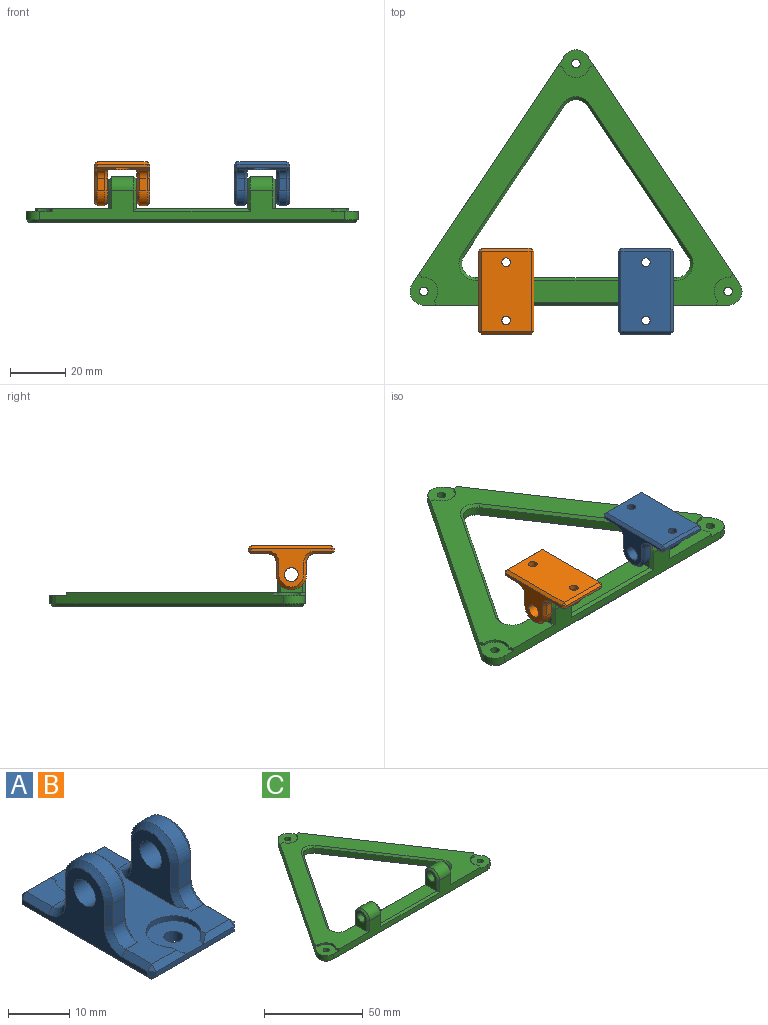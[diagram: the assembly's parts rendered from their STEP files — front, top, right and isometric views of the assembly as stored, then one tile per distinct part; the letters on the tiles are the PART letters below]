
ASSEMBLY  parts=3 mates=5
PART A: 74 faces, bbox 20.7x33.9x16.7 mm
  f0: bspline ~5.16x3.38mm, area 1.7mm2, adj f11,f19,f20,f35
  f1: bspline ~5.16x3.38mm, area 1.7mm2, adj f11,f22,f23,f56
  f2: plane 7.27x1.01mm, normal (0,0.71,0.71), area 8.9mm2, adj f11,f14,f38,f73
  f3: plane 7.27x1.01mm, normal (0,-0.71,0.71), area 8.9mm2, adj f11,f12,f53,f72
  f4: plane 4.5x2.75mm, normal (0,1,0), area 12.4mm2, adj f6,f26,f52,f68
  f5: plane 4.5x2.75mm, normal (0,-1,0), area 12.4mm2, adj f6,f27,f58,f70
  f6: cylinder r=5.5mm len=11mm, axis (-1,0,0), area 47.5mm2, adj f4,f5,f55,f69
  f7: cylinder r=2.5mm len=5mm, axis (-1,0,0), area 74.6mm2, adj f17,f24
  f8: plane 4.5x2.75mm, normal (0,1,0), area 12.4mm2, adj f9,f28,f33,f63
  f9: cylinder r=5.5mm len=11mm, axis (-1,0,0), area 47.5mm2, adj f8,f10,f36,f64
  f10: plane 4.5x2.75mm, normal (0,-1,0), area 12.4mm2, adj f9,f29,f39,f65
  f11: plane 29.74x18.74mm, normal (0,0,1), area 274.6mm2, adj f0,f1,f2,f3,f20,f23,f24,f25
  f12: plane 18x1mm, normal (0,-1,0), area 18mm2, adj f3,f22,f49,f50,f56,f57
  f13: plane 29x18mm, normal (0,0,-1), area 506.9mm2, adj f18,f21,f40,f41,f50,f51
  f14: plane 18x1mm, normal (0,1,0), area 18mm2, adj f2,f19,f34,f35,f41,f42
  f15: cylinder r=2.5mm len=5mm, axis (-1,0,0), area 74.6mm2, adj f16,f25
  f16: plane 29x14mm, normal (1,0,0), area 124.5mm2, adj f15,f30,f31,f33,f34,f36,f39,f40
  f17: plane 29x14mm, normal (-1,0,0), area 124.5mm2, adj f7,f42,f43,f47,f51,f52,f55,f57
  f18: cylinder r=1.55mm len=3.1mm, axis (0,0,1), area 19.5mm2, adj f13,f19
  f19: plane 9.6x9.08mm, normal (0,0,1), area 58.7mm2, adj f0,f14,f18,f20,f73
  f20: cylinder r=4.5mm len=9mm, axis (0,0,1), area 22.2mm2, adj f0,f11,f19,f73
  f21: cylinder r=1.55mm len=3.1mm, axis (0,0,1), area 19.5mm2, adj f13,f22
  f22: plane 9.6x9.08mm, normal (0,0,1), area 58.7mm2, adj f1,f12,f21,f23,f72
  f23: cylinder r=4.5mm len=9mm, axis (0,0,1), area 22.2mm2, adj f1,f11,f22,f72
  f24: plane 12x11.71mm, normal (1,0,0), area 82.2mm2, adj f7,f11,f67,f68,f69,f70,f71
  f25: plane 12x11.71mm, normal (-1,0,0), area 82.2mm2, adj f11,f15,f62,f63,f64,f65,f66
  f26: cylinder r=3mm len=3mm, axis (-1,0,0), area 13mm2, adj f4,f11,f47,f67
  f27: cylinder r=3mm len=3mm, axis (1,0,0), area 13mm2, adj f5,f11,f60,f71
  f28: cylinder r=3mm len=3mm, axis (-1,0,0), area 13mm2, adj f8,f11,f31,f62
  f29: cylinder r=3mm len=3mm, axis (1,0,0), area 13mm2, adj f10,f11,f44,f66
  f30: plane 6x1mm, normal (0.71,0,0.71), area 8.5mm2, adj f11,f16,f31,f32
  f31: cone r=4mm half-angle=45deg, axis (1,0,0), area 7.8mm2, adj f16,f28,f30,f33
  f32: plane 1x1mm, normal (0.58,0.58,0.58), area 0.9mm2, adj f30,f34,f35
  f33: plane 4.5x1mm, normal (0.71,0.71,0), area 6.4mm2, adj f8,f16,f31,f36
  f34: plane 1x1mm, normal (0.71,0.71,0), area 1.4mm2, adj f14,f16,f32,f37
  f35: plane 7.27x1.01mm, normal (0,0.71,0.71), area 8.9mm2, adj f0,f11,f14,f32
  f36: cone r=5.5mm half-angle=45deg, axis (-1,0,0), area 22.2mm2, adj f9,f16,f33,f39
  f37: plane 1x1mm, normal (0.58,0.58,-0.58), area 0.9mm2, adj f34,f40,f41
  f38: plane 1x1mm, normal (-0.58,0.58,0.58), area 0.9mm2, adj f2,f42,f43
  f39: plane 4.5x1mm, normal (0.71,-0.71,0), area 6.4mm2, adj f10,f16,f36,f44
  f40: plane 29x1mm, normal (0.71,0,-0.71), area 41mm2, adj f13,f16,f37,f45
  f41: plane 18x1mm, normal (0,0.71,-0.71), area 25.5mm2, adj f13,f14,f37,f46
  f42: plane 1x1mm, normal (-0.71,0.71,0), area 1.4mm2, adj f14,f17,f38,f46
  f43: plane 6x1mm, normal (-0.71,0,0.71), area 8.5mm2, adj f11,f17,f38,f47
  f44: cone r=4mm half-angle=45deg, axis (1,0,0), area 7.8mm2, adj f16,f29,f39,f48
  f45: plane 1x1mm, normal (0.58,-0.58,-0.58), area 0.9mm2, adj f40,f49,f50
  f46: plane 1x1mm, normal (-0.58,0.58,-0.58), area 0.9mm2, adj f41,f42,f51
  f47: cone r=4mm half-angle=45deg, axis (-1,0,0), area 7.8mm2, adj f17,f26,f43,f52
  f48: plane 6x1mm, normal (0.71,0,0.71), area 8.5mm2, adj f11,f16,f44,f53
  f49: plane 1x1mm, normal (0.71,-0.71,0), area 1.4mm2, adj f12,f16,f45,f53
  f50: plane 18x1mm, normal (0,-0.71,-0.71), area 25.5mm2, adj f12,f13,f45,f54
  f51: plane 29x1mm, normal (-0.71,0,-0.71), area 41mm2, adj f13,f17,f46,f54
  f52: plane 4.5x1mm, normal (-0.71,0.71,0), area 6.4mm2, adj f4,f17,f47,f55
  f53: plane 1x1mm, normal (0.58,-0.58,0.58), area 0.9mm2, adj f3,f48,f49
  f54: plane 1x1mm, normal (-0.58,-0.58,-0.58), area 0.9mm2, adj f50,f51,f57
  f55: cone r=4.5mm half-angle=45deg, axis (1,0,0), area 22.2mm2, adj f6,f17,f52,f58
  f56: plane 7.27x1.01mm, normal (0,-0.71,0.71), area 8.9mm2, adj f1,f11,f12,f59
  f57: plane 1x1mm, normal (-0.71,-0.71,0), area 1.4mm2, adj f12,f17,f54,f59
  f58: plane 4.5x1mm, normal (-0.71,-0.71,0), area 6.4mm2, adj f5,f17,f55,f60
  f59: plane 1x1mm, normal (-0.58,-0.58,0.58), area 0.9mm2, adj f56,f57,f61
  f60: cone r=4mm half-angle=45deg, axis (-1,0,0), area 7.8mm2, adj f17,f27,f58,f61
  f61: plane 6x1mm, normal (-0.71,0,0.71), area 8.5mm2, adj f11,f17,f59,f60
  f62: cone r=4mm half-angle=45deg, axis (-1,0,0), area 5.9mm2, adj f11,f25,f28,f63
  f63: plane 4.5x1mm, normal (-0.71,0.71,0), area 6.4mm2, adj f8,f25,f62,f64
  f64: cone r=4.5mm half-angle=45deg, axis (1,0,0), area 22.2mm2, adj f9,f25,f63,f65
  f65: plane 4.5x1mm, normal (-0.71,-0.71,0), area 6.4mm2, adj f10,f25,f64,f66
  f66: cone r=4mm half-angle=45deg, axis (-1,0,0), area 5.9mm2, adj f11,f25,f29,f65
  f67: cone r=4mm half-angle=45deg, axis (1,0,0), area 5.9mm2, adj f11,f24,f26,f68
  f68: plane 4.5x1mm, normal (0.71,0.71,0), area 6.4mm2, adj f4,f24,f67,f69
  f69: cone r=5.5mm half-angle=45deg, axis (-1,0,0), area 22.2mm2, adj f6,f24,f68,f70
  f70: plane 4.5x1mm, normal (0.71,-0.71,0), area 6.4mm2, adj f5,f24,f69,f71
  f71: cone r=4mm half-angle=45deg, axis (1,0,0), area 5.9mm2, adj f11,f24,f27,f70
  f72: bspline ~5.16x3.38mm, area 1.7mm2, adj f3,f11,f22,f23
  f73: bspline ~5.16x3.38mm, area 1.7mm2, adj f2,f11,f19,f20
PART B: same geometry as A
PART C: 74 faces, bbox 120x92.3x16.5 mm
  f0: plane 72.58x10.5mm, normal (0,1,0), area 337.7mm2, adj f2,f4,f13,f25,f34,f35,f43,f44
  f1: plane 110x10.5mm, normal (0,-1,0), area 493.1mm2, adj f2,f10,f11,f14,f17,f23,f25,f32
  f2: cylinder r=5mm len=10mm, axis (-1,0,0), area 125.7mm2, adj f0,f1,f41,f46
  f3: cylinder r=2.5mm len=10mm, axis (-1,0,0), area 157.1mm2, adj f28,f30
  f4: cylinder r=5mm len=7.78mm, axis (0,0,-1), area 32.4mm2, adj f0,f5,f42,f62
  f5: plane 54.3x36.29mm, normal (0.83,-0.56,0), area 195.9mm2, adj f4,f6,f40,f60
  f6: cylinder r=5mm len=8.31mm, axis (0,0,-1), area 29.5mm2, adj f5,f7,f38,f59
  f7: plane 54.3x36.29mm, normal (-0.83,-0.56,0), area 195.9mm2, adj f6,f13,f37,f61
  f8: cylinder r=5mm len=8.31mm, axis (0,0,-1), area 29.5mm2, adj f9,f12,f20,f53
  f9: plane 82.3x55mm, normal (-0.83,0.56,0), area 387mm2, adj f8,f10,f14,f20,f23,f54,f68,f73
  f10: cylinder r=5mm len=7.78mm, axis (0,0,-1), area 32.4mm2, adj f1,f9,f23,f56
  f11: cylinder r=5mm len=7.78mm, axis (0,0,-1), area 32.4mm2, adj f1,f12,f17,f57
  f12: plane 82.3x55mm, normal (0.83,0.56,0), area 387mm2, adj f8,f11,f14,f17,f20,f55,f69,f71
  f13: cylinder r=5mm len=7.78mm, axis (0,0,-1), area 32.4mm2, adj f0,f7,f36,f63
  f14: plane 113.34x86.36mm, normal (0,0,1), area 2052.2mm2, adj f1,f9,f12,f18,f21,f24,f27,f28
  f15: plane 118x90.3mm, normal (0,0,-1), area 2444.4mm2, adj f53,f54,f55,f56,f57,f58,f59,f60
  f16: cylinder r=1.55mm len=3.1mm, axis (0,0,1), area 29.2mm2, adj f17,f65
  f17: plane 11.5x10mm, normal (0,0,1), area 76.1mm2, adj f1,f11,f12,f16,f18,f70,f71
  f18: cylinder r=5mm len=8.33mm, axis (0,0,1), area 12.2mm2, adj f14,f17,f70,f71
  f19: cylinder r=1.55mm len=3.1mm, axis (0,0,1), area 29.2mm2, adj f20,f66
  f20: plane 13.28x10mm, normal (0,0,1), area 76.1mm2, adj f8,f9,f12,f19,f21,f68,f69
  f21: cylinder r=5mm len=9.68mm, axis (0,0,1), area 13.2mm2, adj f14,f20,f68,f69
  f22: cylinder r=1.55mm len=3.1mm, axis (0,0,1), area 29.2mm2, adj f23,f67
  f23: plane 11.5x10mm, normal (0,0,1), area 76.1mm2, adj f1,f9,f10,f22,f24,f72,f73
  f24: cylinder r=5mm len=8.33mm, axis (0,0,1), area 12.2mm2, adj f14,f23,f72,f73
  f25: cylinder r=5mm len=10mm, axis (-1,0,0), area 125.7mm2, adj f0,f1,f33,f51
  f26: cylinder r=2.5mm len=10mm, axis (-1,0,0), area 157.1mm2, adj f27,f31
  f27: plane 10.5x8mm, normal (1,0,0), area 57.5mm2, adj f14,f26,f32,f33,f34
  f28: plane 10.5x8mm, normal (-1,0,0), area 57.5mm2, adj f3,f14,f39,f41,f43
  f29: plane 40x8mm, normal (0,0,1), area 320mm2, adj f30,f31,f47,f50
  f30: plane 10.5x8mm, normal (1,0,0), area 57.5mm2, adj f3,f29,f45,f46,f48
  f31: plane 10.5x8mm, normal (-1,0,0), area 57.5mm2, adj f26,f29,f49,f51,f52
  f32: plane 6.5x1mm, normal (0.71,-0.71,0), area 9.2mm2, adj f1,f14,f27,f33
  f33: cone r=5mm half-angle=45deg, axis (-1,0,0), area 20mm2, adj f25,f27,f32,f34
  f34: plane 7.5x1mm, normal (0.71,0.71,0), area 9.9mm2, adj f0,f27,f33,f35
  f35: plane 7.29x1mm, normal (0,0.71,0.71), area 9.6mm2, adj f0,f14,f34,f36
  f36: cone r=5mm half-angle=45deg, axis (0,0,1), area 16.8mm2, adj f13,f14,f35,f37
  f37: plane 54.86x37.12mm, normal (-0.59,-0.39,0.71), area 92.4mm2, adj f7,f14,f36,f38
  f38: cone r=5mm half-angle=45deg, axis (0,0,1), area 15.3mm2, adj f6,f14,f37,f40
  f39: plane 6.5x1mm, normal (-0.71,-0.71,0), area 9.2mm2, adj f1,f14,f28,f41
  f40: plane 54.86x37.12mm, normal (0.59,-0.39,0.71), area 92.4mm2, adj f5,f14,f38,f42
  f41: cone r=4mm half-angle=45deg, axis (1,0,0), area 20mm2, adj f2,f28,f39,f43
  f42: cone r=5mm half-angle=45deg, axis (0,0,1), area 16.8mm2, adj f4,f14,f40,f44
  f43: plane 7.5x1mm, normal (-0.71,0.71,0), area 9.9mm2, adj f0,f28,f41,f44
  f44: plane 7.29x1mm, normal (0,0.71,0.71), area 9.6mm2, adj f0,f14,f42,f43
  f45: plane 7.5x1mm, normal (0.71,0.71,0), area 9.9mm2, adj f0,f30,f46,f47
  f46: cone r=5mm half-angle=45deg, axis (-1,0,0), area 20mm2, adj f2,f30,f45,f48
  f47: plane 42x1mm, normal (0,0.71,0.71), area 58mm2, adj f0,f29,f45,f49
  f48: plane 7.5x1mm, normal (0.71,-0.71,0), area 9.9mm2, adj f1,f30,f46,f50
  f49: plane 7.5x1mm, normal (-0.71,0.71,0), area 9.9mm2, adj f0,f31,f47,f51
  f50: plane 42x1mm, normal (0,-0.71,0.71), area 58mm2, adj f1,f29,f48,f52
  f51: cone r=4mm half-angle=45deg, axis (1,0,0), area 20mm2, adj f25,f31,f49,f52
  f52: plane 7.5x1mm, normal (-0.71,-0.71,0), area 9.9mm2, adj f1,f31,f50,f51
  f53: cone r=4mm half-angle=45deg, axis (0,0,1), area 12.5mm2, adj f8,f15,f54,f55
  f54: plane 82.86x55.83mm, normal (-0.59,0.39,-0.71), area 140mm2, adj f9,f15,f53,f56
  f55: plane 82.86x55.83mm, normal (0.59,0.39,-0.71), area 140mm2, adj f12,f15,f53,f57
  f56: cone r=4mm half-angle=45deg, axis (0,0,1), area 13.7mm2, adj f10,f15,f54,f58
  f57: cone r=4mm half-angle=45deg, axis (0,0,1), area 13.7mm2, adj f11,f15,f55,f58
  f58: plane 110x1mm, normal (0,-0.71,-0.71), area 155.6mm2, adj f1,f15,f56,f57
  f59: cone r=6mm half-angle=45deg, axis (0,0,-1), area 15.3mm2, adj f6,f15,f60,f61
  f60: plane 54.86x37.12mm, normal (0.59,-0.39,-0.71), area 92.4mm2, adj f5,f15,f59,f62
  f61: plane 54.86x37.12mm, normal (-0.59,-0.39,-0.71), area 92.4mm2, adj f7,f15,f59,f63
  f62: cone r=6mm half-angle=45deg, axis (0,0,-1), area 16.8mm2, adj f4,f15,f60,f64
  f63: cone r=6mm half-angle=45deg, axis (0,0,-1), area 16.8mm2, adj f13,f15,f61,f64
  f64: plane 72.58x1mm, normal (0,0.71,-0.71), area 102.6mm2, adj f0,f15,f62,f63
  f65: cone r=1.55mm half-angle=45deg, axis (0,0,-1), area 18.2mm2, adj f15,f16
  f66: cone r=1.55mm half-angle=45deg, axis (0,0,-1), area 18.2mm2, adj f15,f19
  f67: cone r=1.55mm half-angle=45deg, axis (0,0,-1), area 18.2mm2, adj f15,f22
  f68: plane 1.8x1mm, normal (0.17,0.99,0), area 1.8mm2, adj f9,f14,f20,f21
  f69: plane 1.8x1mm, normal (-0.17,0.99,0), area 1.8mm2, adj f12,f14,f20,f21
  f70: plane 1.67x1mm, normal (0.91,-0.41,0), area 1.8mm2, adj f1,f14,f17,f18
  f71: plane 1.55x1mm, normal (0.85,-0.53,0), area 1.8mm2, adj f12,f14,f17,f18
  f72: plane 1.67x1mm, normal (-0.91,-0.41,0), area 1.8mm2, adj f1,f14,f23,f24
  f73: plane 1.55x1mm, normal (-0.85,-0.53,0), area 1.8mm2, adj f9,f14,f23,f24
PLACE A rot(axis=(0,1,0),180deg) t=(2.86,-26.03,20.46)mm
PLACE B rot(axis=(-1,0,0),180deg) t=(-47.64,-26.03,20.46)mm
PLACE C t=(-22.39,56.27,1.46)mm fixed
MATE cylindrical C.f2 <-> B.f6  axis (-1,0,0) through (-42.39,-26.03,12.96)mm
MATE planar C.f30 <-> B.f25  axis (1,0,0) through (-42.39,-26.03,10.76)mm
MATE planar A.f6 <-> C.f31  axis (1,0,0) through (-2.39,-26.03,12.96)mm
MATE cylindrical C.f2 <-> A.f6  axis (1,0,0) through (7.61,-26.03,12.96)mm
MATE planar B.f13 <-> A.f13  axis (0,0,1) through (-47.64,-26.03,23.46)mm
